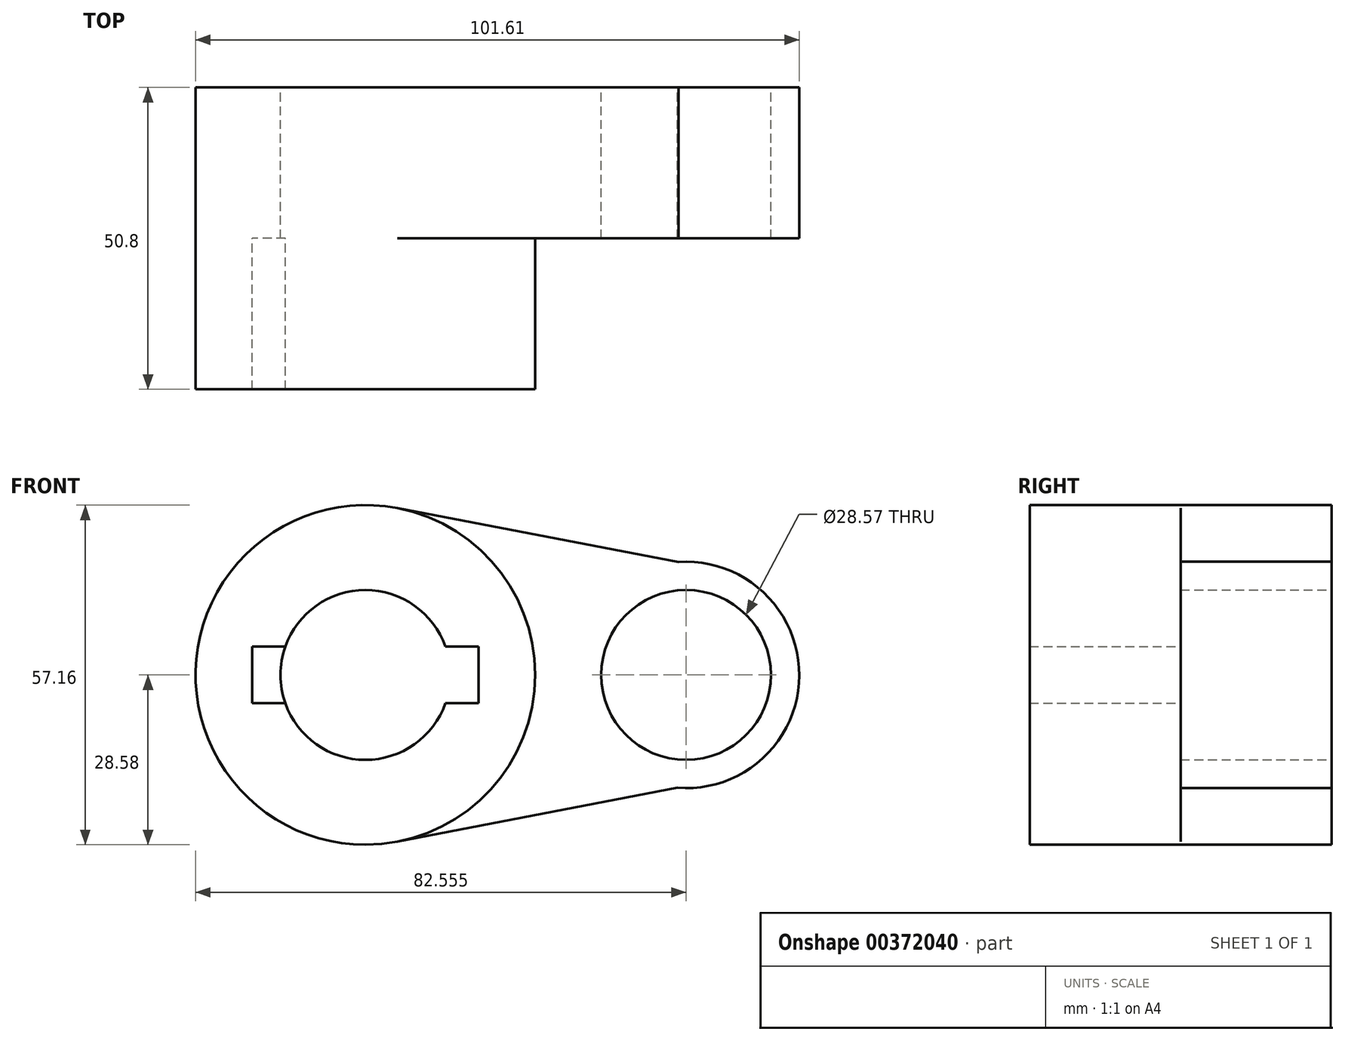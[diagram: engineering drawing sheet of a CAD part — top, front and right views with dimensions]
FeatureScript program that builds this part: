
annotation { "Feature Type Name" : "Feature", "Feature Type Description" : "" }
export const myFeature = defineFeature(function(context is Context, id is Id, definition is map)
    precondition{}
    {
        {
            var Q0;
            Q0=qCreatedBy(makeId("Front.planeOp"),FACE);
            var sketch = newSketch(context, id + "F0", { "sketchPlane" : qUnion([Q0])});
            skCircle(sketch, "E0", {"center": v(0, 0) * mm, "radius": 28.58 * mm});
            skCircle(sketch, "E1", {"center": v(53.98, 0) * mm, "radius": 19.05 * mm});
            skLineSegment(sketch, "E2", {"start": v(52.7, 19) * mm, "end": v(5.37, 28.07) * mm});
            skLineSegment(sketch, "E3", {"start": v(52.51, -19) * mm, "end": v(5.37, -28.07) * mm});
            skCircle(sketch, "E4", {"center": v(0, 0) * mm, "radius": 14.29 * mm});
            skCircle(sketch, "E5", {"center": v(53.98, 0) * mm, "radius": 14.29 * mm});
            skLineSegment(sketch, "E6.bottom", {"start": v(-19.05, 4.76) * mm, "end": v(19.05, 4.76) * mm});
            skLineSegment(sketch, "E6.top", {"start": v(-19.05, -4.76) * mm, "end": v(19.05, -4.76) * mm});
            skLineSegment(sketch, "E6.left", {"start": v(-19.05, 4.76) * mm, "end": v(-19.05, -4.76) * mm});
            skLineSegment(sketch, "E6.right", {"start": v(19.05, 4.76) * mm, "end": v(19.05, -4.76) * mm});
            skSolve(sketch);
        }
        {
            var Q0;
            {var subQ7=sQuery(id+"F0.wireOp",EDGE,"E6.left");Q0=makeQuery(id+"F0.imprint","IMPRINT",FACE,{"disambiguationData":[TD([[makeQuery(id+"F0.imprint","IMPRINT",EDGE,{"derivedFrom":subQ7}),-1.0]])]});}
            var Q1;
            {var subQ0=sQuery(id+"F0.wireOp",EDGE,"E2");Q1=makeQuery(id+"F0.imprint","IMPRINT",FACE,{"disambiguationData":[TD([[makeQuery(id+"F0.imprint","IMPRINT",EDGE,{"derivedFrom":subQ0}),1.0]])]});}
            var Q2;
            Q2=makeQuery(id+"F0.imprint","IMPRINT",FACE,{"disambiguationData":[TD([[makeQuery(id+"F0.imprint","IMPRINT",EDGE,{"derivedFrom":sQuery(id+"F0.wireOp",EDGE,"E5")}),-1.0]])]});
            var Q3;
            {var subQ5=sQuery(id+"F0.wireOp",EDGE,"E6.left");Q3=makeQuery(id+"F0.imprint","IMPRINT",FACE,{"disambiguationData":[TD([[makeQuery(id+"F0.imprint","IMPRINT",EDGE,{"derivedFrom":subQ5}),1.0]])]});}
            extrude(context, id + "F1", {"entities" : qUnion([Q0, Q1, Q2, Q3]), "depth" : 25.4 * mm});
        }
        {
            var Q0;
            {var subQ7=sQuery(id+"F0.wireOp",EDGE,"E6.left");Q0=makeQuery(id+"F0.imprint","IMPRINT",FACE,{"disambiguationData":[TD([[makeQuery(id+"F0.imprint","IMPRINT",EDGE,{"derivedFrom":subQ7}),-1.0]])]});}
            extrude(context, id + "F2", {"entities" : qUnion([Q0]), "operationType" : NewBodyOperationType.ADD, "depth" : 50.8 * mm});
        }
    });
